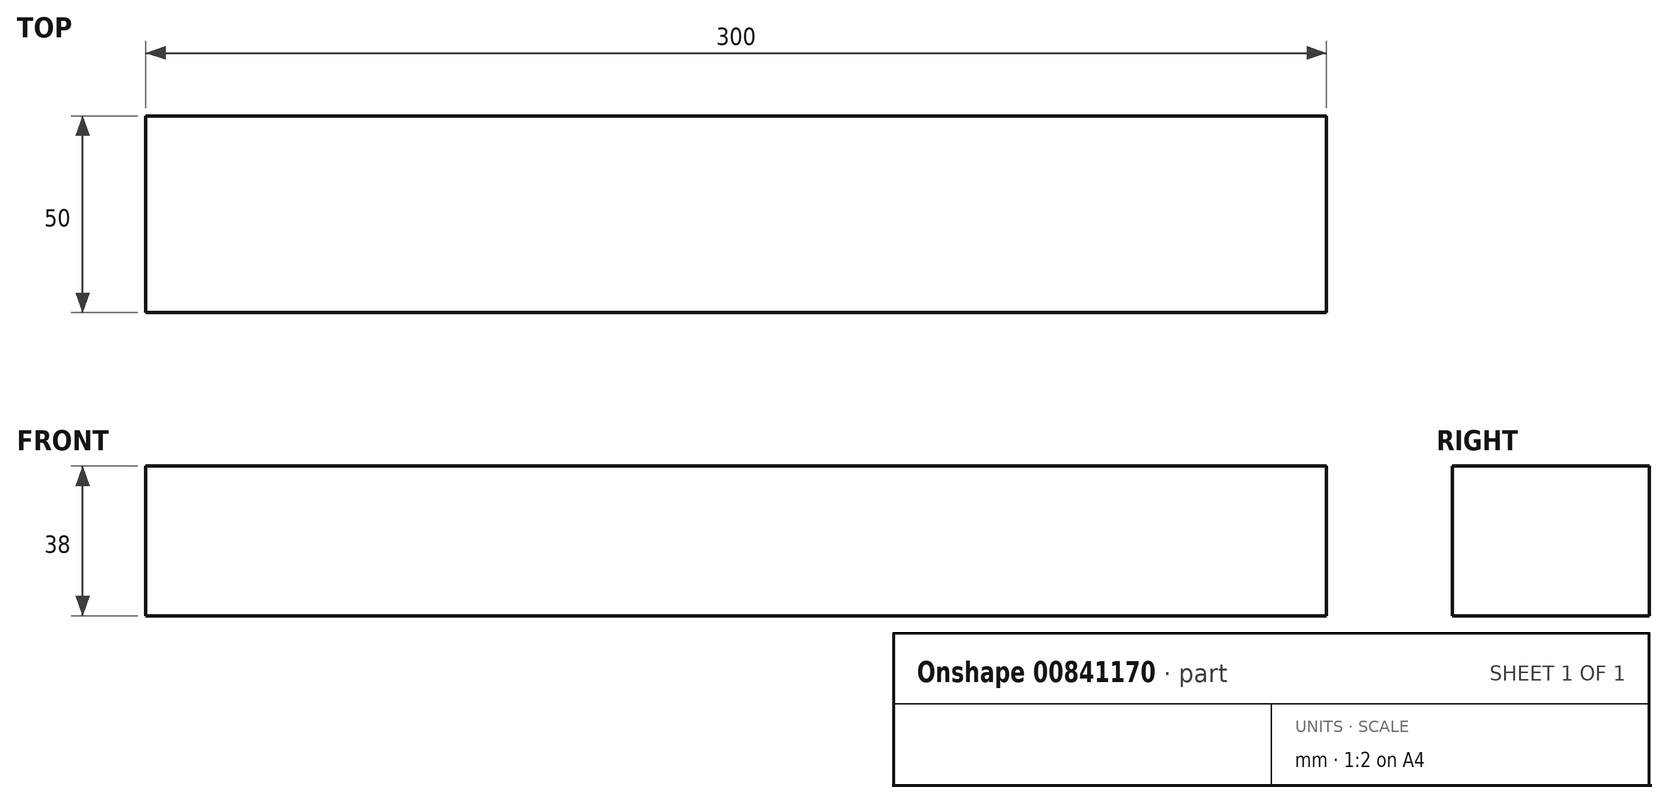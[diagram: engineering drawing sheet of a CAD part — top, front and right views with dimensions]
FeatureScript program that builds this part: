
annotation { "Feature Type Name" : "Feature", "Feature Type Description" : "" }
export const myFeature = defineFeature(function(context is Context, id is Id, definition is map)
    precondition{}
    {
        {
            var Q0;
            Q0=qCreatedBy(makeId("Front.planeOp"),FACE);
            var sketch = newSketch(context, id + "F0", { "sketchPlane" : qUnion([Q0])});
            skLineSegment(sketch, "E0.bottom", {"start": v(0, 38) * mm, "end": v(300, 38) * mm});
            skLineSegment(sketch, "E0.top", {"start": v(0, 0) * mm, "end": v(300, 0) * mm});
            skLineSegment(sketch, "E0.left", {"start": v(0, 38) * mm, "end": v(0, 0) * mm});
            skLineSegment(sketch, "E0.right", {"start": v(300, 38) * mm, "end": v(300, 0) * mm});
            skLineSegment(sketch, "E1", {"start": v(0, 19) * mm, "end": v(300, 19) * mm, "construction": true});
            skSolve(sketch);
        }
        {
            var Q0;
            Q0=makeQuery(id+"F0.imprint","IMPRINT",FACE,{"disambiguationData":[TD([[makeQuery(id+"F0.imprint","IMPRINT",EDGE,{"derivedFrom":sQuery(id+"F0.wireOp",EDGE,"E0.bottom")}),-1.0]])]});
            extrude(context, id + "F1", {"entities" : qUnion([Q0]), "depth" : 50 * mm, "offsetDistance" : 25 * mm});
        }
    });
